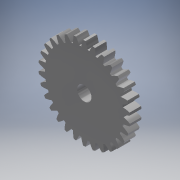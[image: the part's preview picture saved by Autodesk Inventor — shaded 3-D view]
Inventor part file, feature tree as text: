
AUTODESK INVENTOR PART (.ipt)
format: ipt  version: 2019 (Build 230136000, 136)  size: 345,088 bytes
history: native  units: mm (DEFAULTED — no unit token found)
features: other x6, plane x3, sketch x3, extrude x1, hole x1
ambient origin geometry x8: Origin, YZ Plane, XZ Plane, XY Plane, X Axis, Y Axis, Z Axis, Center Point
bodies: Solid1 (feature_tree)
feature tree (14):
  extrude  "Extrusion1"  Depth=2.0mm TaperAngle=0.0deg
  plane  "Work Plane2"
  plane  "Work Plane8"
  plane  "Work Plane9"
  other  "Przekładnia walcowa"
  hole  "Otwór1"  [1 undecoded]
  other  "Edytuj bezpośrednio1"
  sketch  "Sketch1"  dims[d0=16.0mm d1=2.0mm d2=0.0mm]
  sketch  "Sketch2"  dims[d3=15.0mm d4=10.0mm d5=0.0mm d16=10.0mm d17=0.0mm d34=1.047198mm d39=0.0mm d41=0.0mm d43=10.0mm d46=10.0mm d47=0.0mm d48=0.0mm d49=2.5mm d50=6.0mm d51=4.0mm d52=2.0mm d53=90.0deg d54=8.0mm d55=20.594885mm d56=0.0mm d57=0.0mm d58=-0.5mm d59=0.0mm d60=0.0mm d61=0.5mm]
  other  "Srf1"
  sketch  "Szkic3"
  other  "Średnica podziałowa"
  other  "Przesuń1"
  other  "Przesuń2"
note: 1 required parameter value undecoded (feature->parameter linkage not recoverable at this tier; creation-order binding heuristic only, values carry confidence <= 0.55)
